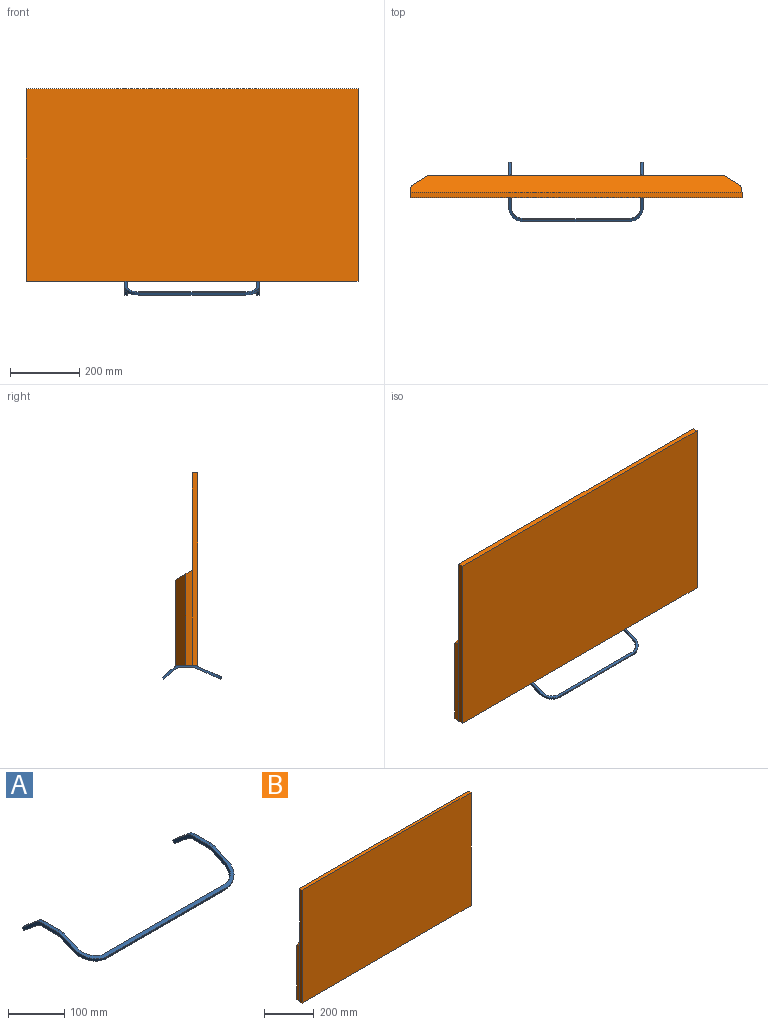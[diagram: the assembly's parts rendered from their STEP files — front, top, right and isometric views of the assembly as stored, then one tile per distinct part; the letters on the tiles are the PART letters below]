
ASSEMBLY  parts=2 mates=1
PART A: 30 faces, bbox 387x171.9x40 mm
  f0: plane 7x5.35mm, normal (0,0.76,-0.65), area 49mm2, adj f1,f2,f3,f4
  f1: plane 34.41x29.1mm, normal (0,0.65,0.76), area 315.4mm2, adj f0,f2,f4,f5
  f2: plane 131.82x40mm, normal (-1,0,0), area 1002.2mm2, adj f0,f1,f3,f5,f6,f7,f8,f9
  f3: plane 34.41x29.1mm, normal (0,-0.65,-0.76), area 315.4mm2, adj f0,f2,f4,f6
  f4: plane 131.82x40mm, normal (1,0,0), area 1002.2mm2, adj f0,f1,f3,f5,f6,f7,f8,f9
  f5: cylinder r=23.5mm len=15.17mm, axis (1,0,0), area 115.5mm2, adj f1,f2,f4,f7
  f6: cylinder r=16.5mm len=10.65mm, axis (1,0,0), area 81.1mm2, adj f2,f3,f4,f8
  f7: plane 38.6x7mm, normal (0,0,1), area 270.2mm2, adj f2,f4,f5,f9
  f8: plane 38.6x7mm, normal (0,0,-1), area 270.2mm2, adj f2,f4,f6,f10
  f9: cylinder r=23.5mm len=9.2mm, axis (1,0,0), area 66.2mm2, adj f2,f4,f7,f11
  f10: cylinder r=16.5mm len=7mm, axis (1,0,0), area 46.5mm2, adj f2,f4,f8,f12
  f11: plane 387x74.47mm, normal (0,-0.39,0.92), area 3503.6mm2, adj f2,f4,f9,f13,f14,f15,f16,f19
  f12: plane 387x74.47mm, normal (0,0.39,-0.92), area 3503.6mm2, adj f2,f4,f10,f13,f14,f15,f16,f19
  f13: cylinder r=43.5mm len=43.5mm, axis (0,-0.39,0.92), area 478.3mm2, adj f2,f11,f12,f15
  f14: cylinder r=36.5mm len=36.5mm, axis (0,-0.39,0.92), area 401.3mm2, adj f4,f11,f12,f16
  f15: plane 300x6.44mm, normal (0,-0.92,-0.39), area 2100mm2, adj f11,f12,f13,f28
  f16: plane 300x6.44mm, normal (0,0.92,0.39), area 2100mm2, adj f11,f12,f14,f29
  f17: plane 7x5.35mm, normal (0,0.76,-0.65), area 49mm2, adj f18,f19,f20,f21
  f18: plane 34.41x29.1mm, normal (0,0.65,0.76), area 315.4mm2, adj f17,f19,f21,f22
  f19: plane 131.82x40mm, normal (1,0,0), area 1002.2mm2, adj f11,f12,f17,f18,f20,f22,f23,f24
  f20: plane 34.41x29.1mm, normal (0,-0.65,-0.76), area 315.4mm2, adj f17,f19,f21,f23
  f21: plane 131.82x40mm, normal (-1,0,0), area 1002.2mm2, adj f11,f12,f17,f18,f20,f22,f23,f24
  f22: cylinder r=23.5mm len=15.17mm, axis (-1,0,0), area 115.5mm2, adj f18,f19,f21,f24
  f23: cylinder r=16.5mm len=10.65mm, axis (-1,0,0), area 81.1mm2, adj f19,f20,f21,f25
  f24: plane 38.6x7mm, normal (0,0,1), area 270.2mm2, adj f19,f21,f22,f26
  f25: plane 38.6x7mm, normal (0,0,-1), area 270.2mm2, adj f19,f21,f23,f27
  f26: cylinder r=23.5mm len=9.2mm, axis (-1,0,0), area 66.2mm2, adj f11,f19,f21,f24
  f27: cylinder r=16.5mm len=7mm, axis (-1,0,0), area 46.5mm2, adj f12,f19,f21,f25
  f28: cylinder r=43.5mm len=43.5mm, axis (0,-0.39,0.92), area 478.3mm2, adj f11,f12,f15,f19
  f29: cylinder r=36.5mm len=36.5mm, axis (0,-0.39,0.92), area 401.3mm2, adj f11,f12,f16,f21
PART B: 12 faces, bbox 956x63x554 mm
  f0: plane 956x15mm, normal (0,0,1), area 14340mm2, adj f1,f5,f6,f7
  f1: plane 956x554mm, normal (0,-1,0), area 529624mm2, adj f0,f2,f6,f7
  f2: plane 956x63mm, normal (0,0,-1), area 58573.2mm2, adj f1,f3,f6,f7,f8,f9,f10,f11
  f3: plane 856x245mm, normal (0,1,0), area 209720mm2, adj f2,f4,f10,f11
  f4: plane 956x48mm, normal (0,0.53,0.85), area 52161.9mm2, adj f3,f5,f8,f9,f10,f11
  f5: plane 956x279mm, normal (0,1,0), area 266724mm2, adj f0,f4,f6,f7
  f6: plane 554x15mm, normal (1,0,0), area 8310mm2, adj f0,f1,f2,f5,f9
  f7: plane 554x15mm, normal (-1,0,0), area 8310mm2, adj f0,f1,f2,f5,f8
  f8: plane 275x18.63mm, normal (-0.98,0.2,0), area 5122.6mm2, adj f2,f4,f7,f10
  f9: plane 275x18.63mm, normal (0.98,0.2,0), area 5122.6mm2, adj f2,f4,f6,f11
  f10: plane 263.36x46.12mm, normal (-0.54,0.84,0), area 13897.5mm2, adj f2,f3,f4,f8
  f11: plane 263.36x46.12mm, normal (0.54,0.84,0), area 13897.5mm2, adj f2,f3,f4,f9
PLACE A t=(0,-530.94,-40)mm
PLACE B t=(0,-530.94,-40)mm
MATE fastened A.f7 <-> B.f2  axis (0,0,-1) through (0,0,0)mm
